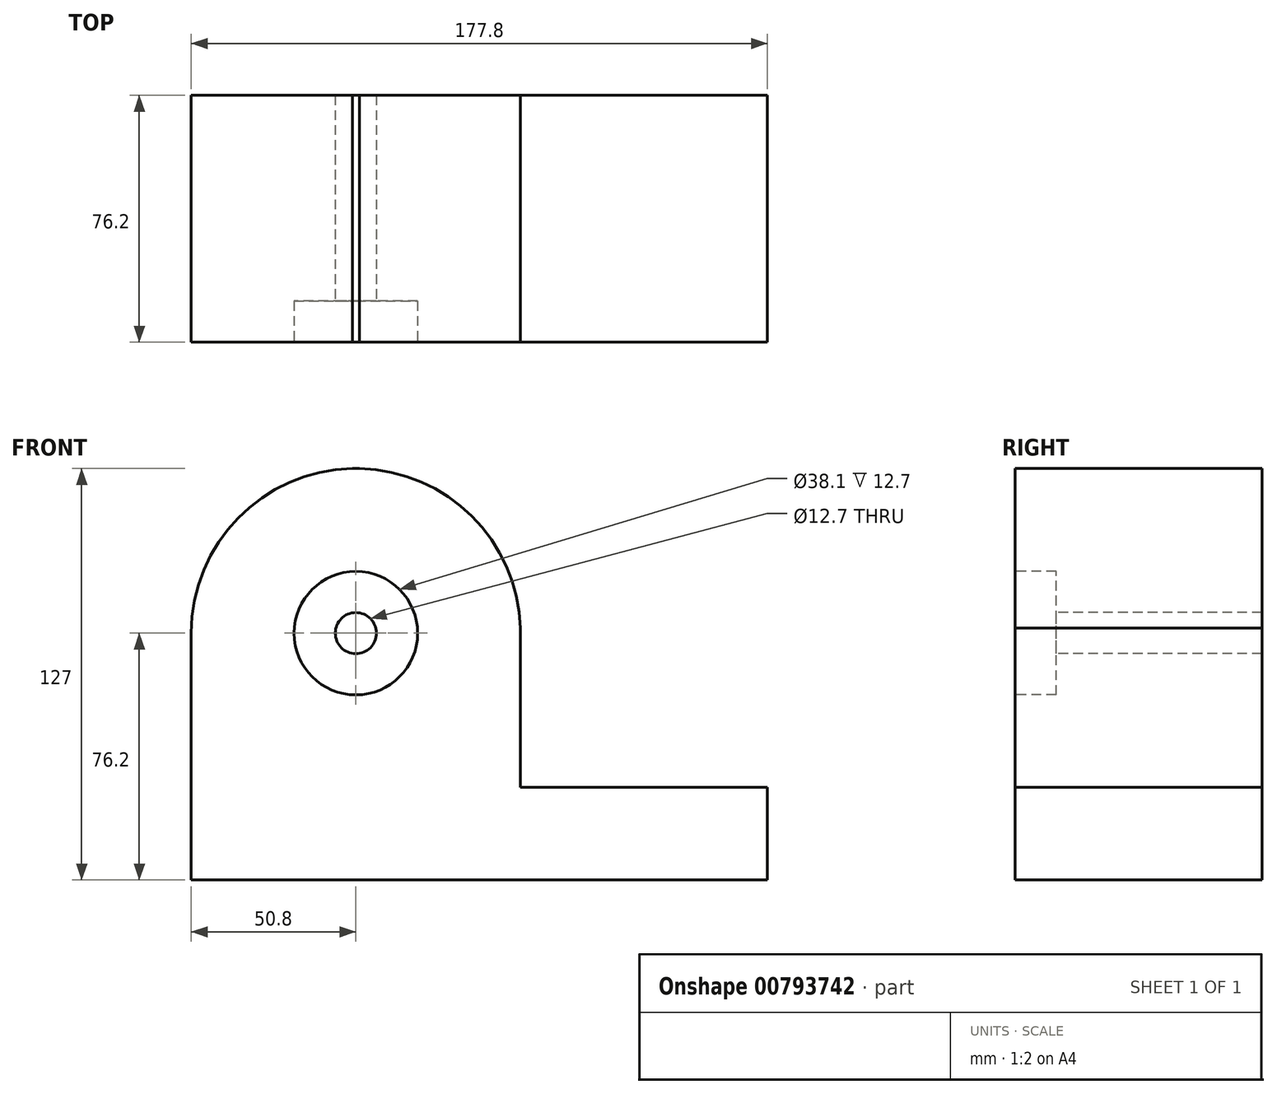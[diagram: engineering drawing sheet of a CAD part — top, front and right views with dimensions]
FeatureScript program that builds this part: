
annotation { "Feature Type Name" : "Feature", "Feature Type Description" : "" }
export const myFeature = defineFeature(function(context is Context, id is Id, definition is map)
    precondition{}
    {
        {
            var Q0;
            Q0=qCreatedBy(makeId("Front.planeOp"),FACE);
            var sketch = newSketch(context, id + "F0", { "sketchPlane" : qUnion([Q0])});
            skLineSegment(sketch, "E0", {"start": v(0, 0) * mm, "end": v(177.8, 0) * mm});
            skLineSegment(sketch, "E1", {"start": v(177.8, 0) * mm, "end": v(177.8, 28.58) * mm});
            skLineSegment(sketch, "E2", {"start": v(0, 0) * mm, "end": v(0, 127) * mm});
            skLineSegment(sketch, "E3", {"start": v(177.8, 28.58) * mm, "end": v(101.6, 28.58) * mm});
            skLineSegment(sketch, "E4", {"start": v(101.6, 28.58) * mm, "end": v(101.6, 127) * mm});
            skLineSegment(sketch, "E5", {"start": v(101.6, 127) * mm, "end": v(0, 127) * mm});
            skSolve(sketch);
        }
        {
            var Q0;
            Q0=makeQuery(id+"F0.imprint","IMPRINT",FACE,{"disambiguationData":[TD([[makeQuery(id+"F0.imprint","IMPRINT",EDGE,{"derivedFrom":sQuery(id+"F0.wireOp",EDGE,"E0")}),1.0]])]});
            extrude(context, id + "F1", {"entities" : qUnion([Q0]), "depth" : 76.2 * mm, "offsetDistance" : 25.4 * mm});
        }
        {
            var Q0;
            Q0=makeQuery(id+"F1.opExtrude","CAP_FACE",FACE,{"disambiguationData":[OSD([sQuery(id+"F0.wireOp",EDGE,"E0"),sQuery(id+"F0.wireOp",EDGE,"E1"),sQuery(id+"F0.wireOp",EDGE,"E2"),sQuery(id+"F0.wireOp",EDGE,"E3"),sQuery(id+"F0.wireOp",EDGE,"E4"),sQuery(id+"F0.wireOp",EDGE,"E5")])],"isStart":false});
            var sketch = newSketch(context, id + "F2", { "sketchPlane" : qUnion([Q0])});
            skLineSegment(sketch, "E6", {"start": v(0, 0) * mm, "end": v(0, 76.2) * mm});
            skLineSegment(sketch, "E7", {"start": v(101.6, 28.58) * mm, "end": v(101.6, 77.79) * mm});
            skArc(sketch, "E8", {"start": v(101.6, 77.79) * mm, "mid": v(50.02, 127) * mm, "end": v(0, 76.2) * mm});
            skCircle(sketch, "E9", {"center": v(50.81, 76.2) * mm, "radius": 19.05 * mm});
            skCircle(sketch, "E10", {"center": v(50.81, 76.2) * mm, "radius": 6.35 * mm});
            skSolve(sketch);
        }
        {
            var Q0;
            {var subQ1=makeQuery(id+"F1.opExtrude","CAP_EDGE",EDGE,{"disambiguationData":[OSD([sQuery(id+"F0.wireOp",EDGE,"E2")])],"isStart":false});var subQ3=makeQuery(id+"F1.opExtrude","CAP_EDGE",EDGE,{"disambiguationData":[OSD([sQuery(id+"F0.wireOp",EDGE,"E5")])],"isStart":false});var subQ5=makeQuery(id+"F2.imprint","INTERSECT",VERTEX,{"derivedFrom":[subQ1,subQ3]});Q0=makeQuery(id+"F2.imprint","IMPRINT",FACE,{"disambiguationData":[TD([[makeQuery(id+"F2.imprint","IMPRINT",EDGE,{"disambiguationData":[TD([[subQ5,1.0]])],"derivedFrom":subQ3}),1.0]])]});}
            var Q1;
            {var subQ1=makeQuery(id+"F1.opExtrude","CAP_EDGE",EDGE,{"disambiguationData":[OSD([sQuery(id+"F0.wireOp",EDGE,"E4")])],"isStart":false});var subQ3=makeQuery(id+"F1.opExtrude","CAP_EDGE",EDGE,{"disambiguationData":[OSD([sQuery(id+"F0.wireOp",EDGE,"E5")])],"isStart":false});var subQ5=makeQuery(id+"F2.imprint","INTERSECT",VERTEX,{"derivedFrom":[subQ1,subQ3]});Q1=makeQuery(id+"F2.imprint","IMPRINT",FACE,{"disambiguationData":[TD([[makeQuery(id+"F2.imprint","IMPRINT",EDGE,{"disambiguationData":[TD([[subQ5,-1.0]])],"derivedFrom":subQ3}),1.0]])]});}
            extrude(context, id + "F3", {"entities" : qUnion([Q0, Q1]), "operationType" : NewBodyOperationType.REMOVE, "endBound" : BoundingType.THROUGH_ALL, "oppositeDirection" : true, "depth" : 25.4 * mm, "offsetDistance" : 25.4 * mm});
        }
        {
            var Q0;
            Q0=makeQuery(id+"F1.opExtrude","CAP_FACE",FACE,{"disambiguationData":[OSD([sQuery(id+"F0.wireOp",EDGE,"E0"),sQuery(id+"F0.wireOp",EDGE,"E1"),sQuery(id+"F0.wireOp",EDGE,"E2"),sQuery(id+"F0.wireOp",EDGE,"E3"),sQuery(id+"F0.wireOp",EDGE,"E4"),sQuery(id+"F0.wireOp",EDGE,"E5")])],"isStart":false});
            var sketch = newSketch(context, id + "F4", { "sketchPlane" : qUnion([Q0])});
            skLineSegment(sketch, "E11", {"start": v(0, 0) * mm, "end": v(0, 76.2) * mm});
            skLineSegment(sketch, "E12", {"start": v(101.6, 28.58) * mm, "end": v(101.6, 76.2) * mm});
            skLineSegment(sketch, "E13", {"start": v(0, 76.2) * mm, "end": v(50.8, 76.2) * mm, "construction": true});
            skCircle(sketch, "E14", {"center": v(50.8, 76.2) * mm, "radius": 19.05 * mm});
            skCircle(sketch, "E15", {"center": v(50.8, 76.2) * mm, "radius": 6.35 * mm});
            skSolve(sketch);
        }
        {
            var Q0;
            Q0=makeQuery(id+"F4.imprint","IMPRINT",FACE,{"disambiguationData":[TD([[makeQuery(id+"F4.imprint","IMPRINT",EDGE,{"derivedFrom":sQuery(id+"F4.wireOp",EDGE,"E14")}),1.0]])]});
            extrude(context, id + "F5", {"entities" : qUnion([Q0]), "operationType" : NewBodyOperationType.REMOVE, "oppositeDirection" : true, "depth" : 12.7 * mm, "offsetDistance" : 25.4 * mm});
        }
        {
            var Q0;
            Q0=makeQuery(id+"F5.boolean.opBoolean","SPLIT",FACE,{"disambiguationData":[TD([makeQuery(id+"F5.opExtrude","SWEPT_FACE",FACE,{"disambiguationData":[OSD([sQuery(id+"F4.wireOp",EDGE,"E15")])]})])],"derivedFrom":makeQuery(id+"F1.opExtrude","CAP_FACE",FACE,{"disambiguationData":[OSD([sQuery(id+"F0.wireOp",EDGE,"E0"),sQuery(id+"F0.wireOp",EDGE,"E1"),sQuery(id+"F0.wireOp",EDGE,"E2"),sQuery(id+"F0.wireOp",EDGE,"E3"),sQuery(id+"F0.wireOp",EDGE,"E4"),sQuery(id+"F0.wireOp",EDGE,"E5")])],"isStart":false})});
            extrude(context, id + "F6", {"entities" : qUnion([Q0]), "operationType" : NewBodyOperationType.REMOVE, "endBound" : BoundingType.THROUGH_ALL, "oppositeDirection" : true, "depth" : 25.4 * mm, "offsetDistance" : 25.4 * mm});
        }
    });
